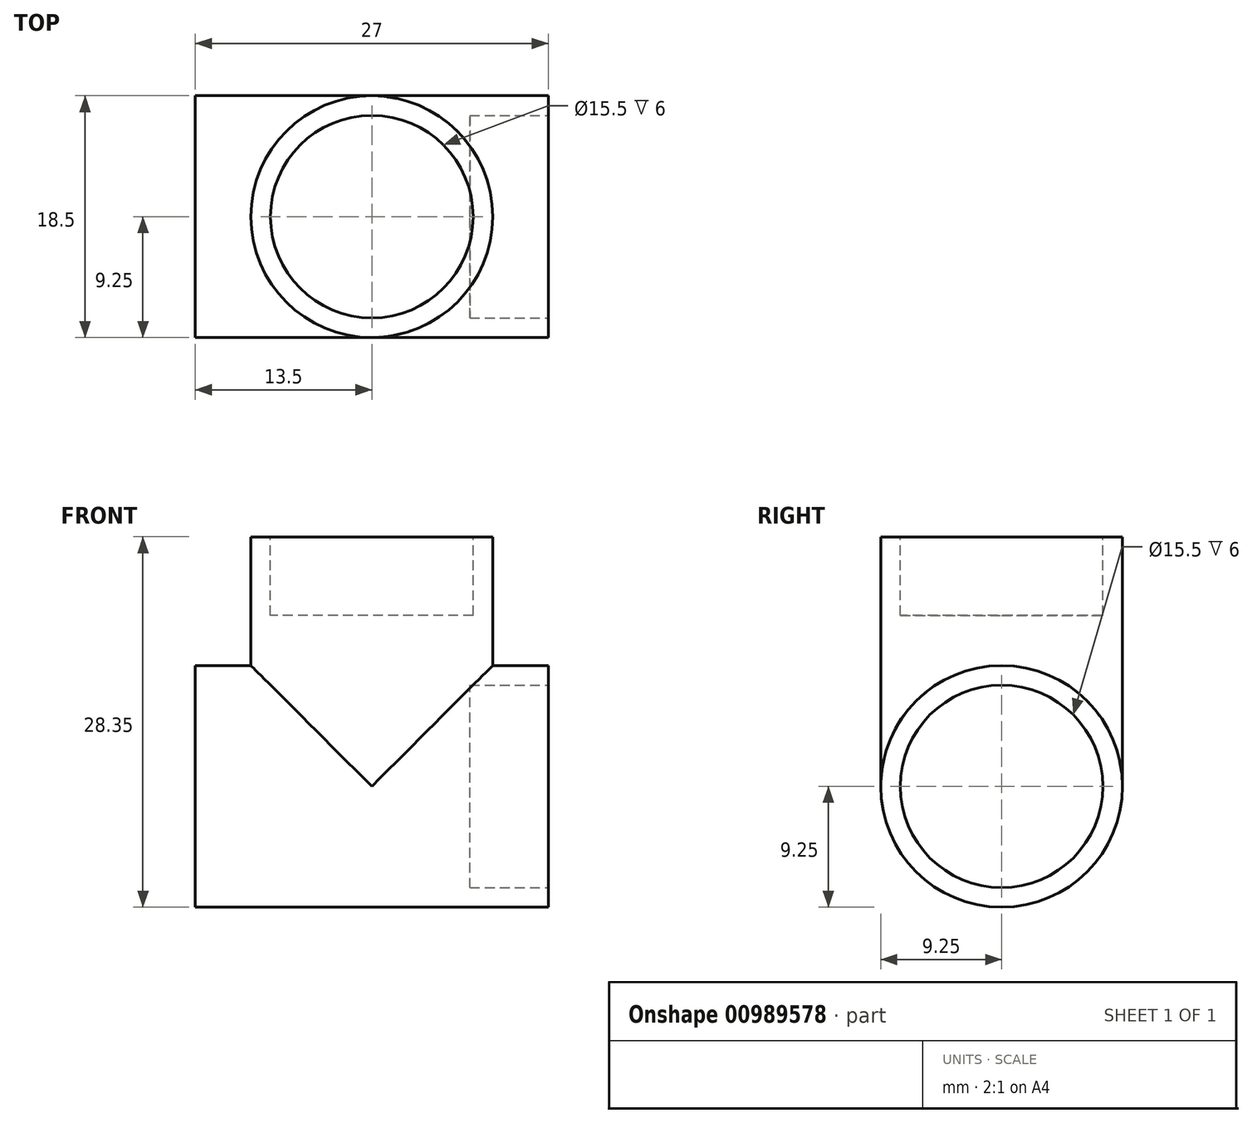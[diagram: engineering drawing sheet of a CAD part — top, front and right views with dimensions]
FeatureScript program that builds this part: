
annotation { "Feature Type Name" : "Feature", "Feature Type Description" : "" }
export const myFeature = defineFeature(function(context is Context, id is Id, definition is map)
    precondition{}
    {
        {
            var Q0;
            Q0=qCreatedBy(makeId("Front.planeOp"),FACE);
            var sketch = newSketch(context, id + "F0", { "sketchPlane" : qUnion([Q0])});
            skLineSegment(sketch, "E0", {"start": v(0, 9.25) * mm, "end": v(13.5, 9.25) * mm});
            skLineSegment(sketch, "E1", {"start": v(13.5, 9.25) * mm, "end": v(13.5, 0) * mm});
            skLineSegment(sketch, "E2", {"start": v(13.5, 0) * mm, "end": v(0, 0) * mm});
            skLineSegment(sketch, "E3", {"start": v(0, 9.25) * mm, "end": v(-13.5, 9.25) * mm});
            skLineSegment(sketch, "E4", {"start": v(-13.5, 9.25) * mm, "end": v(-13.5, 0) * mm});
            skLineSegment(sketch, "E5", {"start": v(-13.5, 0) * mm, "end": v(0, 0) * mm});
            skSolve(sketch);
        }
        {
            var Q0;
            Q0=makeQuery(id+"F0.imprint","IMPRINT",FACE,{"disambiguationData":[TD([[makeQuery(id+"F0.imprint","IMPRINT",EDGE,{"derivedFrom":sQuery(id+"F0.wireOp",EDGE,"E0")}),-1.0]])]});
            var Q1;
            Q1=sQuery(id+"F0.wireOp",EDGE,"E2");
            revolve(context, id + "F1", {"surfaceOperationType" : NewSurfaceOperationType.NEW, "entities" : qUnion([Q0]), "axis" : qUnion([Q1]), "revolveType" : RevolveType.FULL});
        }
        {
            var Q0;
            Q0=qCreatedBy(makeId("Front.planeOp"),FACE);
            var sketch = newSketch(context, id + "F2", { "sketchPlane" : qUnion([Q0])});
            skLineSegment(sketch, "E6", {"start": v(0, 19.1) * mm, "end": v(9.25, 19.1) * mm});
            skLineSegment(sketch, "E7", {"start": v(9.25, 19.1) * mm, "end": v(9.25, 8.35) * mm});
            skLineSegment(sketch, "E8", {"start": v(0, 8.35) * mm, "end": v(0, 19.1) * mm});
            skLineSegment(sketch, "E9", {"start": v(9.25, 8.35) * mm, "end": v(9.25, 0) * mm});
            skLineSegment(sketch, "E10", {"start": v(9.25, 0) * mm, "end": v(0, 0) * mm});
            skLineSegment(sketch, "E11", {"start": v(0, 0) * mm, "end": v(0, 8.35) * mm});
            skSolve(sketch);
        }
        {
            var Q0;
            Q0 = qSketchRegion(id + "F2", true);
            var Q1;
            Q1=sQuery(id+"F2.wireOp",EDGE,"E8");
            revolve(context, id + "F3", {"operationType" : NewBodyOperationType.ADD, "surfaceOperationType" : NewSurfaceOperationType.NEW, "entities" : qUnion([Q0]), "axis" : qUnion([Q1]), "revolveType" : RevolveType.FULL});
        }
        {
            var Q0;
            Q0=makeQuery(id+"F1.opRevolve","SWEPT_FACE",FACE,{"disambiguationData":[OSD([sQuery(id+"F0.wireOp",EDGE,"E1")])]});
            var sketch = newSketch(context, id + "F4", { "sketchPlane" : qUnion([Q0])});
            skCircle(sketch, "E12", {"center": v(0, 0) * mm, "radius": 7.75 * mm});
            skSolve(sketch);
        }
        {
            var Q0;
            Q0=makeQuery(id+"F4.imprint","IMPRINT",FACE,{"disambiguationData":[TD([[makeQuery(id+"F4.imprint","IMPRINT",EDGE,{"derivedFrom":sQuery(id+"F4.wireOp",EDGE,"E12")}),1.0]])]});
            extrude(context, id + "F5", {"entities" : qUnion([Q0]), "operationType" : NewBodyOperationType.REMOVE, "oppositeDirection" : true, "depth" : 6 * mm, "offsetDistance" : 25 * mm});
        }
        {
            var Q0;
            Q0=makeQuery(id+"F3.opRevolve","SWEPT_FACE",FACE,{"disambiguationData":[OSD([sQuery(id+"F2.wireOp",EDGE,"E6")])]});
            var sketch = newSketch(context, id + "F6", { "sketchPlane" : qUnion([Q0])});
            skCircle(sketch, "E13", {"center": v(0, 0) * mm, "radius": 7.75 * mm});
            skSolve(sketch);
        }
        {
            var Q0;
            Q0 = qSketchRegion(id + "F6", true);
            extrude(context, id + "F7", {"entities" : qUnion([Q0]), "operationType" : NewBodyOperationType.REMOVE, "oppositeDirection" : true, "depth" : 6 * mm, "offsetDistance" : 25 * mm});
        }
    });
